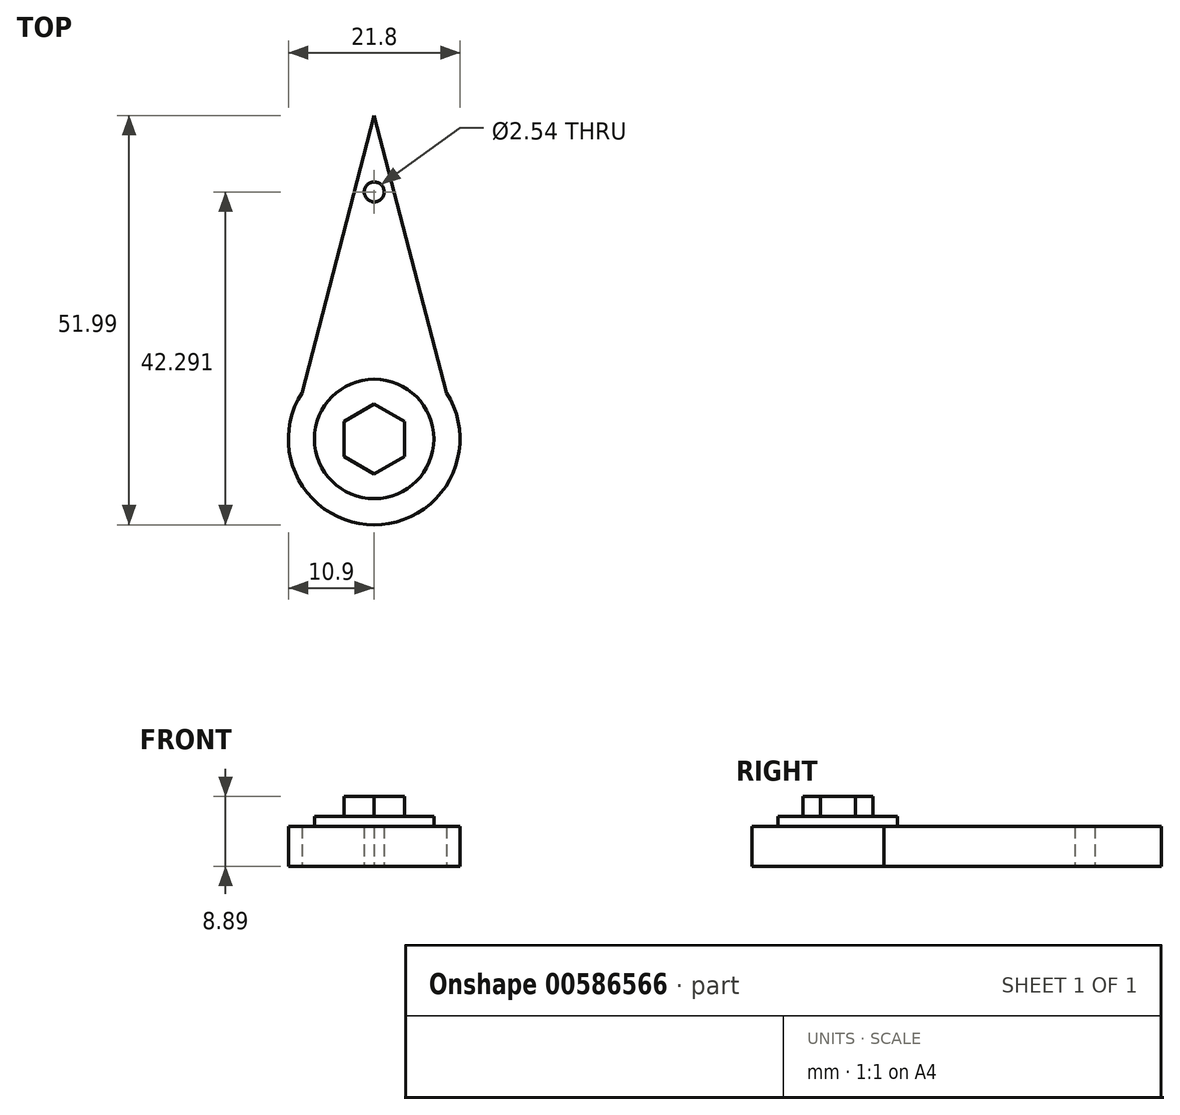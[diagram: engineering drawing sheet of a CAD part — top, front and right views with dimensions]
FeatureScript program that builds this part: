
annotation { "Feature Type Name" : "Feature", "Feature Type Description" : "" }
export const myFeature = defineFeature(function(context is Context, id is Id, definition is map)
    precondition{}
    {
        {
            var Q0;
            Q0=qCreatedBy(makeId("Top.planeOp"),FACE);
            var sketch = newSketch(context, id + "F0", { "sketchPlane" : qUnion([Q0])});
            skCircle(sketch, "E0", {"center": v(0, 0) * mm, "radius": 10.9 * mm});
            skSolve(sketch);
        }
        {
            var Q0;
            Q0=qCreatedBy(makeId("Top.planeOp"),FACE);
            var sketch = newSketch(context, id + "F1", { "sketchPlane" : qUnion([Q0])});
            skLineSegment(sketch, "E1", {"start": v(-10.72, 0) * mm, "end": v(0, 41.09) * mm});
            skLineSegment(sketch, "E2", {"start": v(0, 41.09) * mm, "end": v(10.72, 0) * mm});
            skLineSegment(sketch, "E3", {"start": v(-10.72, 0) * mm, "end": v(10.72, 0) * mm});
            skSolve(sketch);
        }
        {
            var Q0;
            Q0=makeQuery(id+"F1.imprint","IMPRINT",FACE,{"disambiguationData":[TD([[makeQuery(id+"F1.imprint","IMPRINT",EDGE,{"derivedFrom":sQuery(id+"F1.wireOp",EDGE,"E1")}),-1.0]])]});
            var sketch = newSketch(context, id + "F2", { "sketchPlane" : qUnion([Q0])});
            skCircle(sketch, "E4", {"center": v(0, 31.4) * mm, "radius": 1.27 * mm});
            skSolve(sketch);
        }
        {
            var Q0;
            Q0=makeQuery(id+"F2.imprint","IMPRINT",FACE,{"disambiguationData":[TD([[makeQuery(id+"F2.imprint","IMPRINT",EDGE,{"derivedFrom":sQuery(id+"F2.wireOp",EDGE,"E4")}),-1.0]])]});
            extrude(context, id + "F3", {"entities" : qUnion([Q0]), "depth" : 5.08 * mm, "offsetDistance" : 25.4 * mm});
        }
        {
            var Q0;
            Q0=makeQuery(id+"F0.imprint","IMPRINT",FACE,{"disambiguationData":[TD([[makeQuery(id+"F0.imprint","IMPRINT",EDGE,{"derivedFrom":sQuery(id+"F0.wireOp",EDGE,"E0")}),1.0]])]});
            extrude(context, id + "F4", {"entities" : qUnion([Q0]), "operationType" : NewBodyOperationType.ADD, "depth" : 5.08 * mm, "offsetDistance" : 25.4 * mm});
        }
        {
            var Q0;
            Q0=makeQuery(id+"F4.boolean.opBoolean","MERGE",FACE,{"derivedFrom":[makeQuery(id+"F3.opExtrude","CAP_FACE",FACE,{"disambiguationData":[OSD([sQuery(id+"F1.wireOp",EDGE,"E1"),sQuery(id+"F1.wireOp",EDGE,"E2"),sQuery(id+"F1.wireOp",EDGE,"E3"),sQuery(id+"F2.wireOp",EDGE,"E4")])],"isStart":false}),makeQuery(id+"F4.opExtrude","CAP_FACE",FACE,{"disambiguationData":[OSD([sQuery(id+"F0.wireOp",EDGE,"E0")])],"isStart":false})]});
            var sketch = newSketch(context, id + "F5", { "sketchPlane" : qUnion([Q0])});
            skCircle(sketch, "E5", {"center": v(0, 0) * mm, "radius": 7.59 * mm});
            skSolve(sketch);
        }
        {
            var Q0;
            Q0=makeQuery(id+"F5.imprint","IMPRINT",FACE,{"disambiguationData":[TD([[makeQuery(id+"F5.imprint","IMPRINT",EDGE,{"derivedFrom":sQuery(id+"F5.wireOp",EDGE,"E5")}),1.0]])]});
            extrude(context, id + "F6", {"entities" : qUnion([Q0]), "operationType" : NewBodyOperationType.ADD, "depth" : 1.27 * mm, "offsetDistance" : 25.4 * mm});
        }
        {
            var Q0;
            Q0=makeQuery(id+"F6.opExtrude","CAP_FACE",FACE,{"disambiguationData":[OSD([sQuery(id+"F5.wireOp",EDGE,"E5")])],"isStart":false});
            var sketch = newSketch(context, id + "F7", { "sketchPlane" : qUnion([Q0])});
            skCircle(sketch, "E6.cCircle", {"center": v(0, 0) * mm, "radius": 3.83 * mm, "construction": true});
            skLineSegment(sketch, "E6.0", {"start": v(3.83, 2.21) * mm, "end": v(3.83, -2.21) * mm});
            skLineSegment(sketch, "E6.1", {"start": v(3.83, -2.21) * mm, "end": v(0, -4.42) * mm});
            skLineSegment(sketch, "E6.2", {"start": v(0, -4.42) * mm, "end": v(-3.83, -2.21) * mm});
            skLineSegment(sketch, "E6.3", {"start": v(-3.83, -2.21) * mm, "end": v(-3.83, 2.21) * mm});
            skLineSegment(sketch, "E6.4", {"start": v(-3.83, 2.21) * mm, "end": v(0, 4.42) * mm});
            skLineSegment(sketch, "E6.5", {"start": v(0, 4.42) * mm, "end": v(3.83, 2.21) * mm});
            skPoint(sketch, "E6.0.midPoint", {"position": v(3.83, 0) * mm});
            skSolve(sketch);
        }
        {
            var Q0;
            Q0=makeQuery(id+"F7.imprint","IMPRINT",FACE,{"disambiguationData":[TD([[makeQuery(id+"F7.imprint","IMPRINT",EDGE,{"derivedFrom":sQuery(id+"F7.wireOp",EDGE,"E6.0")}),-1.0]])]});
            extrude(context, id + "F8", {"entities" : qUnion([Q0]), "operationType" : NewBodyOperationType.ADD, "depth" : 2.54 * mm, "offsetDistance" : 25.4 * mm});
        }
    });
